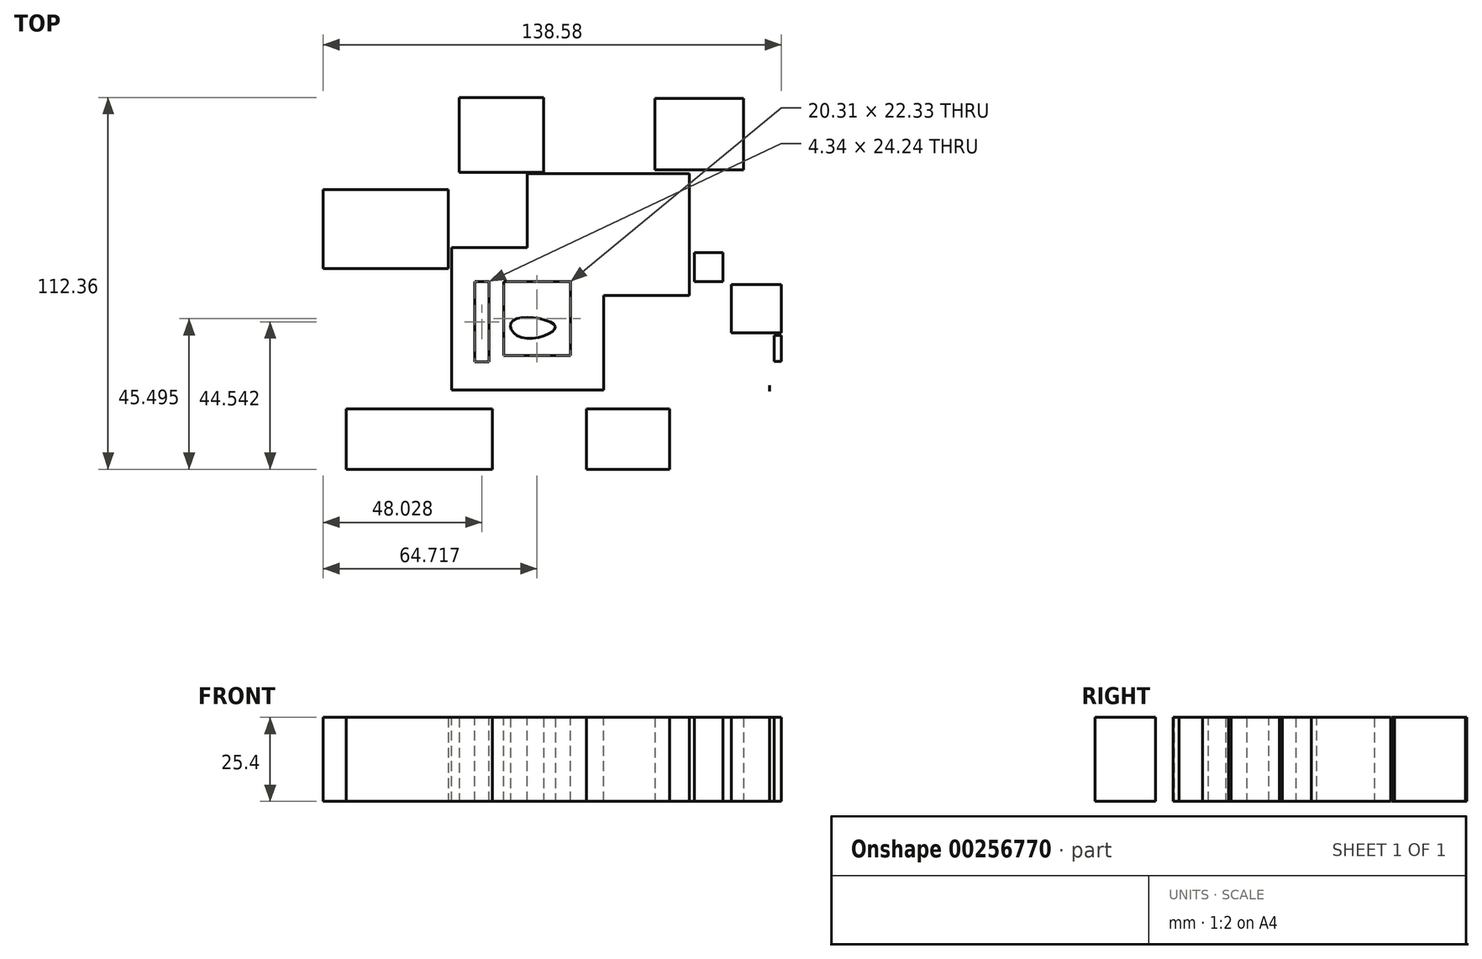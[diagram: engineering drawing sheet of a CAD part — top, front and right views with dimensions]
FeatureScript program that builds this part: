
annotation { "Feature Type Name" : "Feature", "Feature Type Description" : "" }
export const myFeature = defineFeature(function(context is Context, id is Id, definition is map)
    precondition{}
    {
        {
            var Q0;
            Q0=qCreatedBy(makeId("Top.planeOp"),FACE);
            var sketch = newSketch(context, id + "F0", { "sketchPlane" : qUnion([Q0])});
            skLineSegment(sketch, "E0.bottom", {"start": v(-35.94, 32.71) * mm, "end": v(35.94, 32.71) * mm});
            skLineSegment(sketch, "E0.top", {"start": v(-35.94, -32.71) * mm, "end": v(35.94, -32.71) * mm});
            skLineSegment(sketch, "E0.left", {"start": v(-35.94, 32.71) * mm, "end": v(-35.94, -32.71) * mm});
            skLineSegment(sketch, "E0.right", {"start": v(35.94, 32.71) * mm, "end": v(35.94, -32.71) * mm});
            skPoint(sketch, "E0.middle", {"position": v(0, 0) * mm});
            skSolve(sketch);
        }
        {
            var Q0;
            Q0=makeQuery(id+"F0.imprint","IMPRINT",FACE,{"disambiguationData":[TD([[makeQuery(id+"F0.imprint","IMPRINT",EDGE,{"derivedFrom":sQuery(id+"F0.wireOp",EDGE,"E0.bottom")}),-1.0]])]});
            extrude(context, id + "F1", {"entities" : qUnion([Q0]), "depth" : 25.4 * mm});
        }
        {
            var Q0;
            Q0=makeQuery(id+"F1.opExtrude","CAP_FACE",FACE,{"disambiguationData":[OSD([sQuery(id+"F0.wireOp",EDGE,"E0.bottom"),sQuery(id+"F0.wireOp",EDGE,"E0.top"),sQuery(id+"F0.wireOp",EDGE,"E0.left"),sQuery(id+"F0.wireOp",EDGE,"E0.right")])],"isStart":false});
            var sketch = newSketch(context, id + "F2", { "sketchPlane" : qUnion([Q0])});
            skLineSegment(sketch, "E1.bottom", {"start": v(-35.94, 32.71) * mm, "end": v(-13.1, 32.71) * mm});
            skLineSegment(sketch, "E1.top", {"start": v(-35.94, 10.38) * mm, "end": v(-13.1, 10.38) * mm});
            skLineSegment(sketch, "E1.left", {"start": v(-35.94, 32.71) * mm, "end": v(-35.94, 10.38) * mm});
            skLineSegment(sketch, "E1.right", {"start": v(-13.1, 32.71) * mm, "end": v(-13.1, 10.38) * mm});
            skSolve(sketch);
        }
        {
            var Q0;
            Q0 = qSketchRegion(id + "F2", true);
            extrude(context, id + "F3", {"entities" : qUnion([Q0]), "operationType" : NewBodyOperationType.REMOVE, "endBound" : BoundingType.THROUGH_ALL, "oppositeDirection" : true, "depth" : 25.4 * mm});
        }
        {
            var Q0;
            Q0=makeQuery(id+"F1.opExtrude","CAP_FACE",FACE,{"disambiguationData":[OSD([sQuery(id+"F0.wireOp",EDGE,"E0.bottom"),sQuery(id+"F0.wireOp",EDGE,"E0.top"),sQuery(id+"F0.wireOp",EDGE,"E0.left"),sQuery(id+"F0.wireOp",EDGE,"E0.right")])],"isStart":false});
            var sketch = newSketch(context, id + "F4", { "sketchPlane" : qUnion([Q0])});
            skLineSegment(sketch, "E2.bottom", {"start": v(35.94, -32.71) * mm, "end": v(10.04, -32.71) * mm});
            skLineSegment(sketch, "E2.top", {"start": v(35.94, -4.11) * mm, "end": v(10.04, -4.11) * mm});
            skLineSegment(sketch, "E2.left", {"start": v(35.94, -32.71) * mm, "end": v(35.94, -4.11) * mm});
            skLineSegment(sketch, "E2.right", {"start": v(10.04, -32.71) * mm, "end": v(10.04, -4.11) * mm});
            skSolve(sketch);
        }
        {
            var Q0;
            Q0 = qSketchRegion(id + "F4", true);
            extrude(context, id + "F5", {"entities" : qUnion([Q0]), "operationType" : NewBodyOperationType.REMOVE, "endBound" : BoundingType.THROUGH_ALL, "oppositeDirection" : true, "depth" : 25.4 * mm});
        }
        {
            var Q0;
            Q0=makeQuery(id+"F1.opExtrude","CAP_FACE",FACE,{"disambiguationData":[OSD([sQuery(id+"F0.wireOp",EDGE,"E0.bottom"),sQuery(id+"F0.wireOp",EDGE,"E0.top"),sQuery(id+"F0.wireOp",EDGE,"E0.left"),sQuery(id+"F0.wireOp",EDGE,"E0.right")])],"isStart":false});
            var sketch = newSketch(context, id + "F6", { "sketchPlane" : qUnion([Q0])});
            skLineSegment(sketch, "E3.bottom", {"start": v(-20.3, -22.33) * mm, "end": v(0, -22.33) * mm});
            skLineSegment(sketch, "E3.top", {"start": v(-20.3, 0) * mm, "end": v(0, 0) * mm});
            skLineSegment(sketch, "E3.left", {"start": v(-20.3, -22.33) * mm, "end": v(-20.3, 0) * mm});
            skLineSegment(sketch, "E3.right", {"start": v(0, -22.33) * mm, "end": v(0, 0) * mm});
            skSolve(sketch);
        }
        {
            var Q0;
            Q0 = qSketchRegion(id + "F6", true);
            extrude(context, id + "F7", {"entities" : qUnion([Q0]), "operationType" : NewBodyOperationType.REMOVE, "endBound" : BoundingType.THROUGH_ALL, "oppositeDirection" : true, "depth" : 25.4 * mm});
        }
        {
            var Q0;
            Q0=makeQuery(id+"F1.opExtrude","CAP_FACE",FACE,{"disambiguationData":[OSD([sQuery(id+"F0.wireOp",EDGE,"E0.bottom"),sQuery(id+"F0.wireOp",EDGE,"E0.top"),sQuery(id+"F0.wireOp",EDGE,"E0.left"),sQuery(id+"F0.wireOp",EDGE,"E0.right")])],"isStart":false});
            var sketch = newSketch(context, id + "F8", { "sketchPlane" : qUnion([Q0])});
            skLineSegment(sketch, "E4.bottom", {"start": v(-29.01, -24.24) * mm, "end": v(-24.67, -24.24) * mm});
            skLineSegment(sketch, "E4.top", {"start": v(-29.01, 0) * mm, "end": v(-24.67, 0) * mm});
            skLineSegment(sketch, "E4.left", {"start": v(-29.01, -24.24) * mm, "end": v(-29.01, 0) * mm});
            skLineSegment(sketch, "E4.right", {"start": v(-24.67, -24.24) * mm, "end": v(-24.67, 0) * mm});
            skSolve(sketch);
        }
        {
            var Q0;
            Q0 = qSketchRegion(id + "F8", true);
            extrude(context, id + "F9", {"entities" : qUnion([Q0]), "operationType" : NewBodyOperationType.REMOVE, "endBound" : BoundingType.THROUGH_ALL, "oppositeDirection" : true, "depth" : 25.4 * mm});
        }
        {
            var Q0;
            Q0=qCreatedBy(makeId("Top.planeOp"),FACE);
            var sketch = newSketch(context, id + "F10", { "sketchPlane" : qUnion([Q0])});
            skLineSegment(sketch, "E5.bottom", {"start": v(29.96, -38.36) * mm, "end": v(-67.83, -38.36) * mm});
            skLineSegment(sketch, "E5.top", {"start": v(29.96, -56.66) * mm, "end": v(-67.83, -56.66) * mm});
            skLineSegment(sketch, "E5.left", {"start": v(29.96, -38.36) * mm, "end": v(29.96, -56.66) * mm});
            skLineSegment(sketch, "E5.right", {"start": v(-67.83, -38.36) * mm, "end": v(-67.83, -56.66) * mm});
            skSolve(sketch);
        }
        {
            var Q0;
            Q0 = qSketchRegion(id + "F10", true);
            extrude(context, id + "F11", {"entities" : qUnion([Q0]), "depth" : 25.4 * mm});
        }
        {
            var Q0;
            Q0=makeQuery(id+"F11.opExtrude","CAP_FACE",FACE,{"disambiguationData":[OSD([sQuery(id+"F10.wireOp",EDGE,"E5.bottom"),sQuery(id+"F10.wireOp",EDGE,"E5.top"),sQuery(id+"F10.wireOp",EDGE,"E5.left"),sQuery(id+"F10.wireOp",EDGE,"E5.right")])],"isStart":false});
            var sketch = newSketch(context, id + "F12", { "sketchPlane" : qUnion([Q0])});
            skLineSegment(sketch, "E6.bottom", {"start": v(-23.71, -67.81) * mm, "end": v(4.75, -67.81) * mm});
            skLineSegment(sketch, "E6.top", {"start": v(-23.71, -38.36) * mm, "end": v(4.75, -38.36) * mm});
            skLineSegment(sketch, "E6.left", {"start": v(-23.71, -67.81) * mm, "end": v(-23.71, -38.36) * mm});
            skLineSegment(sketch, "E6.right", {"start": v(4.75, -67.81) * mm, "end": v(4.75, -38.36) * mm});
            skSolve(sketch);
        }
        {
            var Q0;
            Q0 = qSketchRegion(id + "F12", true);
            extrude(context, id + "F13", {"entities" : qUnion([Q0]), "operationType" : NewBodyOperationType.REMOVE, "endBound" : BoundingType.THROUGH_ALL, "oppositeDirection" : true, "depth" : 25.4 * mm});
        }
        {
            var Q0;
            Q0=qCreatedBy(makeId("Top.planeOp"),FACE);
            var sketch = newSketch(context, id + "F14", { "sketchPlane" : qUnion([Q0])});
            skLineSegment(sketch, "E7.bottom", {"start": v(-8.22, 33.07) * mm, "end": v(-33.74, 33.07) * mm});
            skLineSegment(sketch, "E7.top", {"start": v(-8.22, 55.7) * mm, "end": v(-33.74, 55.7) * mm});
            skLineSegment(sketch, "E7.left", {"start": v(-8.22, 33.07) * mm, "end": v(-8.22, 55.7) * mm});
            skLineSegment(sketch, "E7.right", {"start": v(-33.74, 33.07) * mm, "end": v(-33.74, 55.7) * mm});
            skSolve(sketch);
        }
        {
            var Q0;
            Q0 = qSketchRegion(id + "F14", true);
            extrude(context, id + "F15", {"entities" : qUnion([Q0]), "depth" : 25.4 * mm});
        }
        {
            var Q0;
            Q0=qCreatedBy(makeId("Top.planeOp"),FACE);
            var sketch = newSketch(context, id + "F16", { "sketchPlane" : qUnion([Q0])});
            skLineSegment(sketch, "E8.bottom", {"start": v(25.44, 33.86) * mm, "end": v(52.3, 33.86) * mm});
            skLineSegment(sketch, "E8.top", {"start": v(25.44, 55.4) * mm, "end": v(52.3, 55.4) * mm});
            skLineSegment(sketch, "E8.left", {"start": v(25.44, 33.86) * mm, "end": v(25.44, 55.4) * mm});
            skLineSegment(sketch, "E8.right", {"start": v(52.3, 33.86) * mm, "end": v(52.3, 55.4) * mm});
            skSolve(sketch);
        }
        {
            var Q0;
            Q0 = qSketchRegion(id + "F16", true);
            extrude(context, id + "F17", {"entities" : qUnion([Q0]), "depth" : 25.4 * mm});
        }
        {
            var Q0;
            Q0=qCreatedBy(makeId("Top.planeOp"),FACE);
            var sketch = newSketch(context, id + "F18", { "sketchPlane" : qUnion([Q0])});
            skLineSegment(sketch, "E9.bottom", {"start": v(37.44, 8.83) * mm, "end": v(46.07, 8.83) * mm});
            skLineSegment(sketch, "E9.top", {"start": v(37.44, 0) * mm, "end": v(46.07, 0) * mm});
            skLineSegment(sketch, "E9.left", {"start": v(37.44, 8.83) * mm, "end": v(37.44, 0) * mm});
            skLineSegment(sketch, "E9.right", {"start": v(46.07, 8.83) * mm, "end": v(46.07, 0) * mm});
            skLineSegment(sketch, "E10.bottom", {"start": v(48.6, -0.83) * mm, "end": v(63.7, -0.83) * mm});
            skLineSegment(sketch, "E10.top", {"start": v(48.6, -15.5) * mm, "end": v(63.7, -15.5) * mm});
            skLineSegment(sketch, "E10.left", {"start": v(48.6, -0.83) * mm, "end": v(48.6, -15.5) * mm});
            skLineSegment(sketch, "E10.right", {"start": v(63.7, -0.83) * mm, "end": v(63.7, -15.5) * mm});
            skLineSegment(sketch, "E11.bottom", {"start": v(63.71, -16.2) * mm, "end": v(61.59, -16.2) * mm});
            skLineSegment(sketch, "E11.top", {"start": v(63.71, -24.1) * mm, "end": v(61.59, -24.1) * mm});
            skLineSegment(sketch, "E11.left", {"start": v(63.71, -16.2) * mm, "end": v(63.71, -24.1) * mm});
            skLineSegment(sketch, "E11.right", {"start": v(61.59, -16.2) * mm, "end": v(61.59, -24.1) * mm});
            skLineSegment(sketch, "E12.bottom", {"start": v(60.18, -31.28) * mm, "end": v(60.19, -31.28) * mm});
            skLineSegment(sketch, "E12.top", {"start": v(60.18, -33.07) * mm, "end": v(60.19, -33.07) * mm});
            skLineSegment(sketch, "E12.left", {"start": v(60.18, -31.28) * mm, "end": v(60.18, -33.07) * mm});
            skLineSegment(sketch, "E12.right", {"start": v(60.19, -31.28) * mm, "end": v(60.19, -33.07) * mm});
            skSolve(sketch);
        }
        {
            var Q0;
            Q0 = qSketchRegion(id + "F18", true);
            extrude(context, id + "F19", {"entities" : qUnion([Q0]), "depth" : 25.4 * mm});
        }
        {
            var Q0;
            Q0=qCreatedBy(makeId("Top.planeOp"),FACE);
            var sketch = newSketch(context, id + "F20", { "sketchPlane" : qUnion([Q0])});
            skLineSegment(sketch, "E13.bottom", {"start": v(-37.06, 4.05) * mm, "end": v(-74.87, 4.05) * mm});
            skLineSegment(sketch, "E13.top", {"start": v(-37.06, 27.85) * mm, "end": v(-74.87, 27.85) * mm});
            skLineSegment(sketch, "E13.left", {"start": v(-37.06, 4.05) * mm, "end": v(-37.06, 27.85) * mm});
            skLineSegment(sketch, "E13.right", {"start": v(-74.87, 4.05) * mm, "end": v(-74.87, 27.85) * mm});
            skSolve(sketch);
        }
        {
            var Q0;
            Q0 = qSketchRegion(id + "F20", true);
            extrude(context, id + "F21", {"entities" : qUnion([Q0]), "depth" : 25.4 * mm});
        }
        {
            var Q0;
            Q0=qCreatedBy(makeId("Top.planeOp"),FACE);
            var sketch = newSketch(context, id + "F22", { "sketchPlane" : qUnion([Q0])});
            skFitSpline(sketch, "E14", {"points": [v(-17.47, -11.72) * mm, v(-14.91, -16.83) * mm, v(-4.69, -13.42) * mm, v(-17.47, -11.72) * mm]});
            skSolve(sketch);
        }
        {
            var Q0;
            Q0 = qSketchRegion(id + "F22", true);
            extrude(context, id + "F23", {"entities" : qUnion([Q0]), "depth" : 25.4 * mm});
        }
    });
